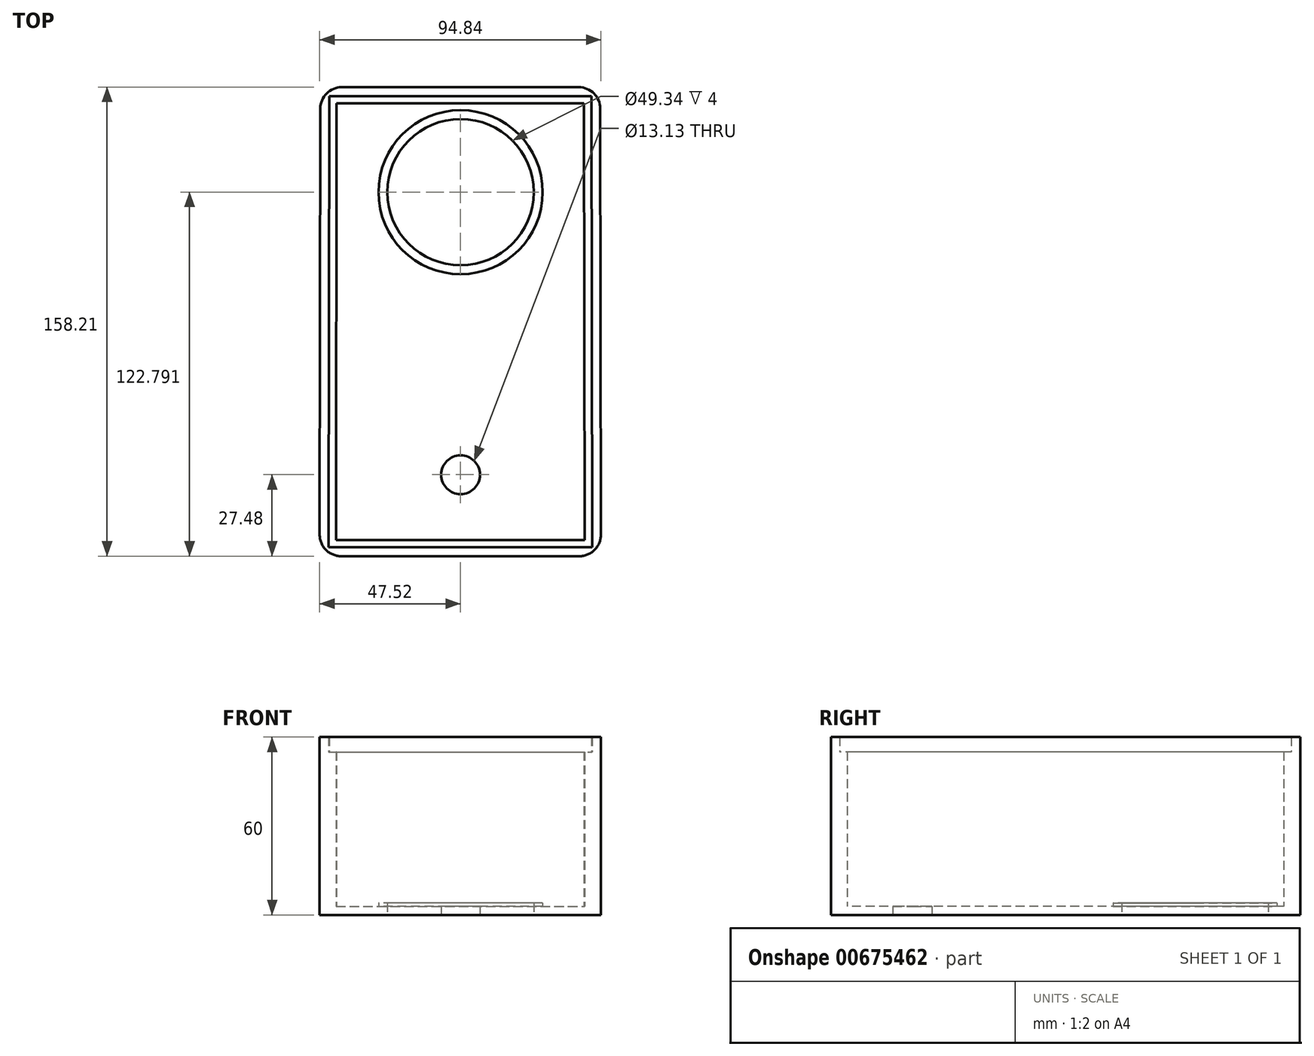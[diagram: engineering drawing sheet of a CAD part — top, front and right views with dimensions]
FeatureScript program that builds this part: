
annotation { "Feature Type Name" : "Feature", "Feature Type Description" : "" }
export const myFeature = defineFeature(function(context is Context, id is Id, definition is map)
    precondition{}
    {
        {
            var Q0;
            Q0=qCreatedBy(makeId("Top.planeOp"),FACE);
            var sketch = newSketch(context, id + "F0", { "sketchPlane" : qUnion([Q0])});
            skLineSegment(sketch, "E0.right", {"start": v(47.1, 80.1) * mm, "end": v(47.33, -78.1) * mm});
            skLineSegment(sketch, "E1.MirrorCS", {"start": v(-47.3, 80.1) * mm, "end": v(-47.53, -78.1) * mm});
            skLineSegment(sketch, "E2", {"start": v(-47.3, 80.1) * mm, "end": v(47.1, 80.1) * mm});
            skLineSegment(sketch, "E3", {"start": v(-47.53, -78.1) * mm, "end": v(47.33, -78.1) * mm});
            skLineSegment(sketch, "E4.0", {"start": v(-44.3, 77.1) * mm, "end": v(44.1, 77.1) * mm});
            skLineSegment(sketch, "E4.1", {"start": v(-44.3, 77.1) * mm, "end": v(-44.53, -75.1) * mm});
            skLineSegment(sketch, "E4.2", {"start": v(-44.53, -75.1) * mm, "end": v(44.33, -75.1) * mm});
            skLineSegment(sketch, "E4.3", {"start": v(44.1, 77.1) * mm, "end": v(44.33, -75.1) * mm});
            skCircle(sketch, "E5", {"center": v(0, 44.68) * mm, "radius": 27.67 * mm});
            skCircle(sketch, "E6.0", {"center": v(0, 44.68) * mm, "radius": 24.67 * mm});
            skCircle(sketch, "E7", {"center": v(0, -50.63) * mm, "radius": 6.57 * mm});
            skLineSegment(sketch, "E8.0", {"start": v(-41.8, 74.6) * mm, "end": v(41.6, 74.6) * mm});
            skLineSegment(sketch, "E8.1", {"start": v(-41.8, 74.6) * mm, "end": v(-42.02, -72.6) * mm});
            skLineSegment(sketch, "E8.2", {"start": v(-42.02, -72.6) * mm, "end": v(41.82, -72.6) * mm});
            skLineSegment(sketch, "E8.3", {"start": v(41.6, 74.6) * mm, "end": v(41.82, -72.6) * mm});
            skSolve(sketch);
        }
        {
            var Q0;
            Q0=makeQuery(id+"F0.imprint","IMPRINT",FACE,{"disambiguationData":[TD([[makeQuery(id+"F0.imprint","IMPRINT",EDGE,{"derivedFrom":sQuery(id+"F0.wireOp",EDGE,"E0.right")}),-1.0]])]});
            extrude(context, id + "F1", {"entities" : qUnion([Q0]), "depth" : 60 * mm, "offsetDistance" : 25 * mm});
        }
        {
            var Q0;
            Q0=makeQuery(id+"F0.imprint","IMPRINT",FACE,{"disambiguationData":[TD([[makeQuery(id+"F0.imprint","IMPRINT",EDGE,{"derivedFrom":sQuery(id+"F0.wireOp",EDGE,"E4.0")}),-1.0]])]});
            extrude(context, id + "F2", {"entities" : qUnion([Q0]), "operationType" : NewBodyOperationType.ADD, "depth" : 55 * mm, "offsetDistance" : 25 * mm});
        }
        {
            var Q0;
            Q0=makeQuery(id+"F0.imprint","IMPRINT",FACE,{"disambiguationData":[TD([[makeQuery(id+"F0.imprint","IMPRINT",EDGE,{"derivedFrom":sQuery(id+"F0.wireOp",EDGE,"E5")}),1.0]])]});
            extrude(context, id + "F3", {"entities" : qUnion([Q0]), "operationType" : NewBodyOperationType.ADD, "depth" : 4 * mm, "offsetDistance" : 25 * mm});
        }
        {
            var Q0;
            Q0=makeQuery(id+"F0.imprint","IMPRINT",FACE,{"disambiguationData":[TD([[makeQuery(id+"F0.imprint","IMPRINT",EDGE,{"derivedFrom":sQuery(id+"F0.wireOp",EDGE,"E5")}),-1.0]])]});
            extrude(context, id + "F4", {"entities" : qUnion([Q0]), "operationType" : NewBodyOperationType.ADD, "depth" : 2.9 * mm, "offsetDistance" : 25 * mm});
        }
        {
            var Q0;
            Q0=makeQuery(id+"F1.opExtrude","SWEPT_EDGE",EDGE,{"disambiguationData":[OSD([sQuery(id+"F0.wireOp",EDGE,"E0.right"),sQuery(id+"F0.wireOp",EDGE,"E3")])]});
            var Q1;
            Q1=makeQuery(id+"F1.opExtrude","SWEPT_EDGE",EDGE,{"disambiguationData":[OSD([sQuery(id+"F0.wireOp",EDGE,"E1.MirrorCS"),sQuery(id+"F0.wireOp",EDGE,"E3")])]});
            var Q2;
            Q2=makeQuery(id+"F1.opExtrude","SWEPT_EDGE",EDGE,{"disambiguationData":[OSD([sQuery(id+"F0.wireOp",EDGE,"E1.MirrorCS"),sQuery(id+"F0.wireOp",EDGE,"E2")])]});
            var Q3;
            Q3=makeQuery(id+"F1.opExtrude","SWEPT_EDGE",EDGE,{"disambiguationData":[OSD([sQuery(id+"F0.wireOp",EDGE,"E0.right"),sQuery(id+"F0.wireOp",EDGE,"E2")])]});
            fillet(context, id + "F5", {"entities" : qUnion([Q0, Q1, Q2, Q3]), "radius" : 7.26 * mm, "tangentPropagation" : true, "allowEdgeOverflow" : false});
        }
    });
